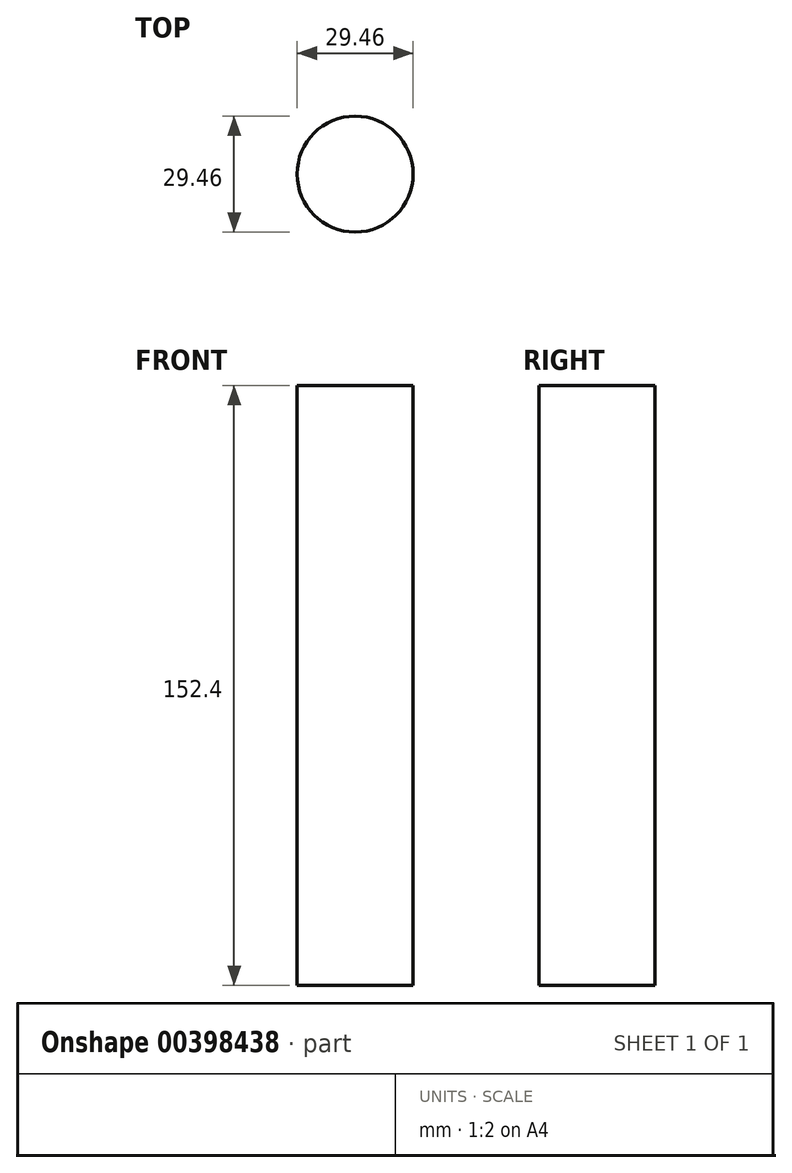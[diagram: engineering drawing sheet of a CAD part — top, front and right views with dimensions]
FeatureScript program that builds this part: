
annotation { "Feature Type Name" : "Feature", "Feature Type Description" : "" }
export const myFeature = defineFeature(function(context is Context, id is Id, definition is map)
    precondition{}
    {
        {
            var Q0;
            Q0=qCreatedBy(makeId("Top.planeOp"),FACE);
            var sketch = newSketch(context, id + "F0", { "sketchPlane" : qUnion([Q0])});
            skCircle(sketch, "E0", {"center": v(0, 0) * mm, "radius": 14.73 * mm});
            skSolve(sketch);
        }
        {
            var Q0;
            Q0=makeQuery(id+"F0.imprint","IMPRINT",FACE,{"disambiguationData":[TD([[makeQuery(id+"F0.imprint","IMPRINT",EDGE,{"derivedFrom":sQuery(id+"F0.wireOp",EDGE,"E0")}),1.0]])]});
            extrude(context, id + "F1", {"entities" : qUnion([Q0]), "depth" : 152.4 * mm});
        }
    });
